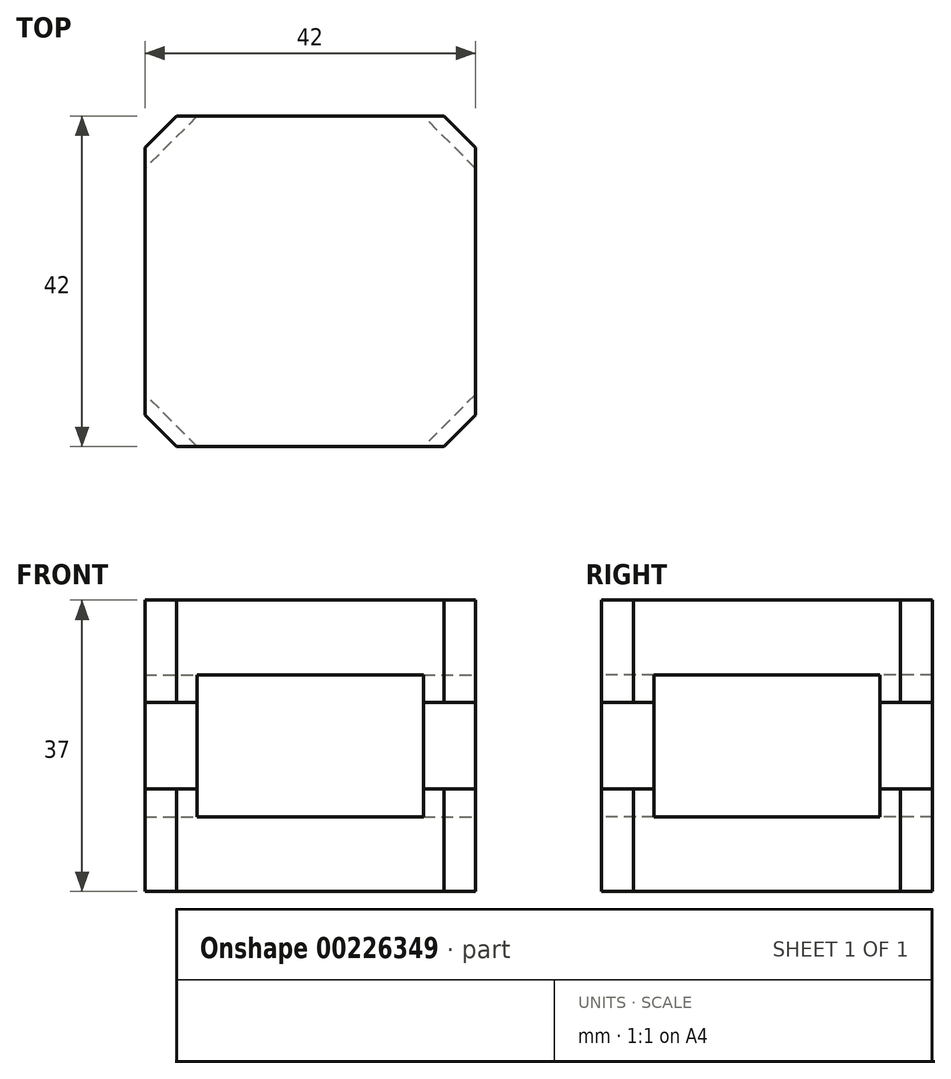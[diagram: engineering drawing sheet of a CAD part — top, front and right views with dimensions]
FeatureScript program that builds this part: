
annotation { "Feature Type Name" : "Feature", "Feature Type Description" : "" }
export const myFeature = defineFeature(function(context is Context, id is Id, definition is map)
    precondition{}
    {
        {
            var Q0;
            Q0=qCreatedBy(makeId("Top.planeOp"),FACE);
            var sketch = newSketch(context, id + "F0", { "sketchPlane" : qUnion([Q0])});
            skLineSegment(sketch, "E0.bottom", {"start": v(16.97, -21) * mm, "end": v(-16.97, -21) * mm});
            skLineSegment(sketch, "E0.top", {"start": v(16.97, 21) * mm, "end": v(-16.97, 21) * mm});
            skLineSegment(sketch, "E0.left", {"start": v(21, -16.97) * mm, "end": v(21, 16.97) * mm});
            skLineSegment(sketch, "E0.right", {"start": v(-21, -16.97) * mm, "end": v(-21, 16.97) * mm});
            skPoint(sketch, "E0.middle", {"position": v(0, 0) * mm});
            skLineSegment(sketch, "E1.bottom", {"start": v(-21, 16.97) * mm, "end": v(-16.97, 21) * mm});
            skLineSegment(sketch, "E1.top", {"start": v(16.97, -21) * mm, "end": v(21, -16.97) * mm});
            skLineSegment(sketch, "E1.left", {"start": v(-21, -16.97) * mm, "end": v(-16.97, -21) * mm});
            skLineSegment(sketch, "E1.right", {"start": v(16.97, 21) * mm, "end": v(21, 16.97) * mm});
            skLineSegment(sketch, "E2", {"start": v(21, 0) * mm, "end": v(0, 0) * mm, "construction": true});
            skLineSegment(sketch, "E3", {"start": v(0, 21) * mm, "end": v(0, 0) * mm, "construction": true});
            skSolve(sketch);
        }
        {
            var Q0;
            Q0 = qSketchRegion(id + "F0", true);
            extrude(context, id + "F1", {"entities" : qUnion([Q0]), "depth" : 13 * mm});
        }
        {
            var Q0;
            Q0=qCreatedBy(makeId("Top.planeOp"),FACE);
            cPlane(context, id + "F2", {"entities" : qUnion([Q0]), "cplaneType" : CPlaneType.OFFSET, "offset" : 9.5 * mm, "width" : 150 * mm, "height" : 150 * mm});
        }
        {
            var Q0;
            Q0=qCreatedBy(id+"F2.planeOp",FACE);
            var sketch = newSketch(context, id + "F3", { "sketchPlane" : qUnion([Q0])});
            skLineSegment(sketch, "E4.bottom", {"start": v(14.36, -21) * mm, "end": v(-14.36, -21) * mm});
            skLineSegment(sketch, "E4.top", {"start": v(14.36, 21) * mm, "end": v(-14.36, 21) * mm});
            skLineSegment(sketch, "E4.left", {"start": v(21, -14.36) * mm, "end": v(21, 14.36) * mm});
            skLineSegment(sketch, "E4.right", {"start": v(-21, -14.36) * mm, "end": v(-21, 14.36) * mm});
            skPoint(sketch, "E4.middle", {"position": v(0, 0) * mm});
            skLineSegment(sketch, "E5.bottom", {"start": v(-21, 14.36) * mm, "end": v(-14.36, 21) * mm});
            skLineSegment(sketch, "E5.top", {"start": v(14.36, -21) * mm, "end": v(21, -14.36) * mm});
            skLineSegment(sketch, "E5.left", {"start": v(-21, -14.36) * mm, "end": v(-14.36, -21) * mm});
            skLineSegment(sketch, "E5.right", {"start": v(14.36, 21) * mm, "end": v(21, 14.36) * mm});
            skLineSegment(sketch, "E6", {"start": v(21, 0) * mm, "end": v(0, 0) * mm, "construction": true});
            skLineSegment(sketch, "E7", {"start": v(0, 21) * mm, "end": v(0, 0) * mm, "construction": true});
            skSolve(sketch);
        }
        {
            var Q0;
            Q0 = qSketchRegion(id + "F3", true);
            extrude(context, id + "F4", {"entities" : qUnion([Q0]), "depth" : 18 * mm});
        }
        {
            var Q0;
            Q0=makeQuery(id+"F4.opExtrude","SWEPT_BODY",BODY,{"disambiguationData":[OSD([sQuery(id+"F3.wireOp",EDGE,"E4.bottom"),sQuery(id+"F3.wireOp",EDGE,"E4.top"),sQuery(id+"F3.wireOp",EDGE,"E4.left"),sQuery(id+"F3.wireOp",EDGE,"E4.right"),sQuery(id+"F3.wireOp",EDGE,"E5.bottom"),sQuery(id+"F3.wireOp",EDGE,"E5.top"),sQuery(id+"F3.wireOp",EDGE,"E5.left"),sQuery(id+"F3.wireOp",EDGE,"E5.right")])]});
            var Q1;
            Q1=makeQuery(id+"F1.opExtrude","SWEPT_BODY",BODY,{"disambiguationData":[OSD([sQuery(id+"F0.wireOp",EDGE,"E0.bottom"),sQuery(id+"F0.wireOp",EDGE,"E0.top"),sQuery(id+"F0.wireOp",EDGE,"E0.left"),sQuery(id+"F0.wireOp",EDGE,"E0.right"),sQuery(id+"F0.wireOp",EDGE,"E1.bottom"),sQuery(id+"F0.wireOp",EDGE,"E1.top"),sQuery(id+"F0.wireOp",EDGE,"E1.left"),sQuery(id+"F0.wireOp",EDGE,"E1.right")])]});
            booleanBodies(context, id + "F5", {"operationType" : BooleanOperationType.SUBTRACTION, "tools" : qUnion([Q0]), "targets" : qUnion([Q1]), "keepTools" : true});
        }
        {
            var Q0;
            Q0=makeQuery(id+"F4.opExtrude","CAP_FACE",FACE,{"disambiguationData":[OSD([sQuery(id+"F3.wireOp",EDGE,"E4.bottom"),sQuery(id+"F3.wireOp",EDGE,"E4.top"),sQuery(id+"F3.wireOp",EDGE,"E4.left"),sQuery(id+"F3.wireOp",EDGE,"E4.right"),sQuery(id+"F3.wireOp",EDGE,"E5.bottom"),sQuery(id+"F3.wireOp",EDGE,"E5.top"),sQuery(id+"F3.wireOp",EDGE,"E5.left"),sQuery(id+"F3.wireOp",EDGE,"E5.right")])],"isStart":false});
            cPlane(context, id + "F6", {"entities" : qUnion([Q0]), "cplaneType" : CPlaneType.OFFSET, "offset" : 3.5 * mm, "oppositeDirection" : true, "width" : 150 * mm, "height" : 150 * mm});
        }
        {
            var Q0;
            Q0=qCreatedBy(id+"F6.planeOp",FACE);
            var sketch = newSketch(context, id + "F7", { "sketchPlane" : qUnion([Q0])});
            skLineSegment(sketch, "E8.bottom", {"start": v(16.97, -21) * mm, "end": v(-16.97, -21) * mm});
            skLineSegment(sketch, "E8.top", {"start": v(16.97, 21) * mm, "end": v(-16.97, 21) * mm});
            skLineSegment(sketch, "E8.left", {"start": v(21, -16.97) * mm, "end": v(21, 16.97) * mm});
            skLineSegment(sketch, "E8.right", {"start": v(-21, -16.97) * mm, "end": v(-21, 16.97) * mm});
            skPoint(sketch, "E8.middle", {"position": v(0, 0) * mm});
            skLineSegment(sketch, "E9.bottom", {"start": v(-21, 16.97) * mm, "end": v(-16.97, 21) * mm});
            skLineSegment(sketch, "E9.top", {"start": v(16.97, -21) * mm, "end": v(21, -16.97) * mm});
            skLineSegment(sketch, "E9.left", {"start": v(-21, -16.97) * mm, "end": v(-16.97, -21) * mm});
            skLineSegment(sketch, "E9.right", {"start": v(16.97, 21) * mm, "end": v(21, 16.97) * mm});
            skLineSegment(sketch, "E10", {"start": v(21, 0) * mm, "end": v(0, 0) * mm, "construction": true});
            skLineSegment(sketch, "E11", {"start": v(0, 21) * mm, "end": v(0, 0) * mm, "construction": true});
            skSolve(sketch);
        }
        {
            var Q0;
            Q0 = qSketchRegion(id + "F7", true);
            extrude(context, id + "F8", {"entities" : qUnion([Q0]), "depth" : 13 * mm});
        }
        {
            var Q0;
            Q0=makeQuery(id+"F4.opExtrude","SWEPT_BODY",BODY,{"disambiguationData":[OSD([sQuery(id+"F3.wireOp",EDGE,"E4.bottom"),sQuery(id+"F3.wireOp",EDGE,"E4.top"),sQuery(id+"F3.wireOp",EDGE,"E4.left"),sQuery(id+"F3.wireOp",EDGE,"E4.right"),sQuery(id+"F3.wireOp",EDGE,"E5.bottom"),sQuery(id+"F3.wireOp",EDGE,"E5.top"),sQuery(id+"F3.wireOp",EDGE,"E5.left"),sQuery(id+"F3.wireOp",EDGE,"E5.right")])]});
            var Q1;
            Q1=makeQuery(id+"F8.opExtrude","SWEPT_BODY",BODY,{"disambiguationData":[OSD([sQuery(id+"F7.wireOp",EDGE,"E8.bottom"),sQuery(id+"F7.wireOp",EDGE,"E8.top"),sQuery(id+"F7.wireOp",EDGE,"E8.left"),sQuery(id+"F7.wireOp",EDGE,"E8.right"),sQuery(id+"F7.wireOp",EDGE,"E9.bottom"),sQuery(id+"F7.wireOp",EDGE,"E9.top"),sQuery(id+"F7.wireOp",EDGE,"E9.left"),sQuery(id+"F7.wireOp",EDGE,"E9.right")])]});
            booleanBodies(context, id + "F9", {"operationType" : BooleanOperationType.SUBTRACTION, "tools" : qUnion([Q0]), "targets" : qUnion([Q1]), "keepTools" : true});
        }
    });
